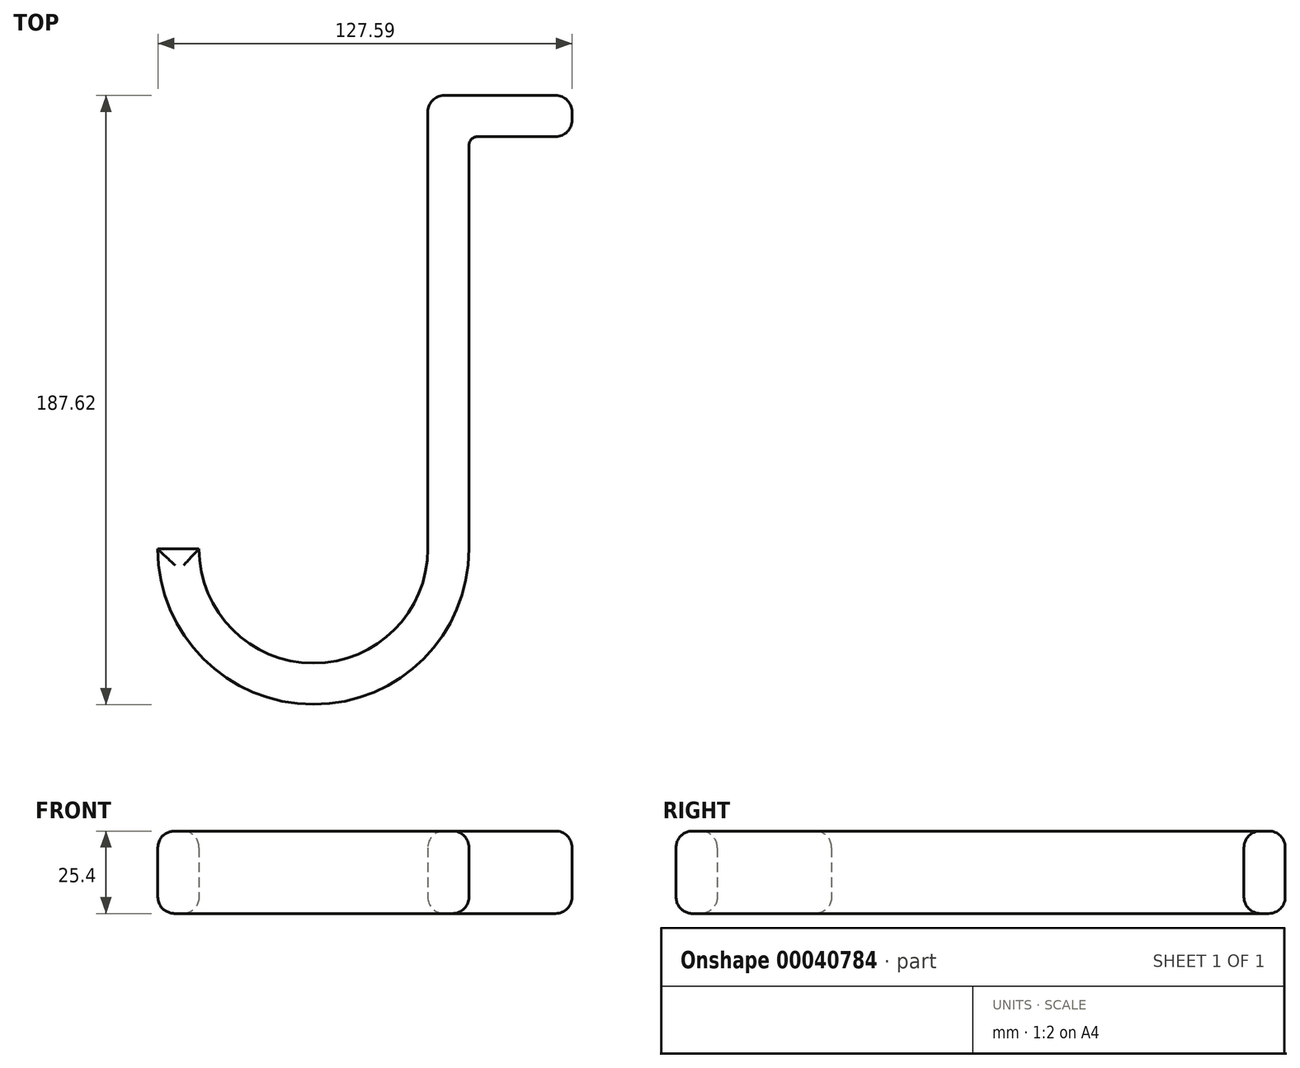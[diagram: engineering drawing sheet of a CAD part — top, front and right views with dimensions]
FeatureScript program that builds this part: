
annotation { "Feature Type Name" : "Feature", "Feature Type Description" : "" }
export const myFeature = defineFeature(function(context is Context, id is Id, definition is map)
    precondition{}
    {
        {
            var Q0;
            Q0=qCreatedBy(makeId("Top.planeOp"),FACE);
            var sketch = newSketch(context, id + "F0", { "sketchPlane" : qUnion([Q0])});
            skLineSegment(sketch, "E0.bottom", {"start": v(-7.23, 31.41) * mm, "end": v(5.47, 31.41) * mm});
            skLineSegment(sketch, "E0.left", {"start": v(-7.23, 31.41) * mm, "end": v(-7.23, -95.59) * mm});
            skLineSegment(sketch, "E0.right", {"start": v(5.47, 31.41) * mm, "end": v(5.47, -95.59) * mm});
            skLineSegment(sketch, "E1.bottom", {"start": v(-7.23, 44.11) * mm, "end": v(37.22, 44.11) * mm});
            skLineSegment(sketch, "E1.top", {"start": v(-7.23, 31.41) * mm, "end": v(37.22, 31.41) * mm});
            skLineSegment(sketch, "E1.left", {"start": v(-7.23, 44.11) * mm, "end": v(-7.23, 31.41) * mm});
            skLineSegment(sketch, "E1.right", {"start": v(37.22, 44.11) * mm, "end": v(37.22, 31.41) * mm});
            skLineSegment(sketch, "E2.bottom", {"start": v(24.52, 31.41) * mm, "end": v(37.22, 31.41) * mm});
            skLineSegment(sketch, "E2.top", {"start": v(24.52, -6.69) * mm, "end": v(37.22, -6.69) * mm});
            skLineSegment(sketch, "E2.left", {"start": v(24.52, 31.41) * mm, "end": v(24.52, -6.69) * mm});
            skLineSegment(sketch, "E2.right", {"start": v(37.22, 31.41) * mm, "end": v(37.22, -6.69) * mm});
            skArc(sketch, "E3", {"start": v(-77.67, -95.59) * mm, "mid": v(-42.45, -130.8) * mm, "end": v(-7.23, -95.59) * mm});
            skArc(sketch, "E4", {"start": v(-90.37, -95.59) * mm, "mid": v(-42.45, -143.5) * mm, "end": v(5.47, -95.59) * mm});
            skLineSegment(sketch, "E5", {"start": v(-77.67, -95.59) * mm, "end": v(-90.37, -95.59) * mm});
            skPoint(sketch, "E6.end.orphan", {"position": v(-42.45, -108.29) * mm});
            skSolve(sketch);
        }
        {
            var Q0;
            {var subQ1=sQuery(id+"F0.wireOp",EDGE,"E0.left");Q0=makeQuery(id+"F0.imprint","IMPRINT",FACE,{"disambiguationData":[TD([[makeQuery(id+"F0.imprint","IMPRINT",EDGE,{"derivedFrom":subQ1}),1.0]])]});}
            var Q1;
            Q1=makeQuery(id+"F0.imprint","IMPRINT",FACE,{"disambiguationData":[TD([[makeQuery(id+"F0.imprint","IMPRINT",EDGE,{"derivedFrom":sQuery(id+"F0.wireOp",EDGE,"E1.bottom")}),-1.0]])]});
            var Q2;
            Q2=makeQuery(id+"F0.imprint","IMPRINT",FACE,{"disambiguationData":[TD([[makeQuery(id+"F0.imprint","IMPRINT",EDGE,{"derivedFrom":sQuery(id+"F0.wireOp",EDGE,"E2.bottom")}),-1.0]])]});
            extrude(context, id + "F1", {"entities" : qUnion([Q0, Q1, Q2]), "depth" : 25.4 * mm});
        }
        {
            var Q0;
            Q0=makeQuery(id+"F1.opExtrude","SWEPT_EDGE",EDGE,{"disambiguationData":[OSD([sQuery(id+"F0.wireOp",EDGE,"E2.top"),sQuery(id+"F0.wireOp",EDGE,"E2.right")])]});
            var Q1;
            Q1=makeQuery(id+"F1.opExtrude","SWEPT_EDGE",EDGE,{"disambiguationData":[OSD([sQuery(id+"F0.wireOp",EDGE,"E2.top"),sQuery(id+"F0.wireOp",EDGE,"E2.left")])]});
            var Q2;
            Q2=makeQuery(id+"F1.opExtrude","SWEPT_EDGE",EDGE,{"disambiguationData":[OSD([sQuery(id+"F0.wireOp",EDGE,"E1.bottom"),sQuery(id+"F0.wireOp",EDGE,"E1.right")])]});
            var Q3;
            Q3=makeQuery(id+"F1.opExtrude","SWEPT_EDGE",EDGE,{"disambiguationData":[OSD([sQuery(id+"F0.wireOp",EDGE,"E1.bottom"),sQuery(id+"F0.wireOp",EDGE,"E1.left")])]});
            fillet(context, id + "F2", {"entities" : qUnion([Q0, Q1, Q2, Q3]), "radius" : 5.08 * mm, "tangentPropagation" : true, "allowEdgeOverflow" : false});
        }
        {
            var Q0;
            Q0=makeQuery(id+"F1.opExtrude","SWEPT_EDGE",EDGE,{"disambiguationData":[OSD([sQuery(id+"F0.wireOp",EDGE,"E0.right"),sQuery(id+"F0.wireOp",EDGE,"E1.top")])]});
            var Q1;
            Q1=makeQuery(id+"F1.opExtrude","SWEPT_EDGE",EDGE,{"disambiguationData":[OSD([sQuery(id+"F0.wireOp",EDGE,"E1.top"),sQuery(id+"F0.wireOp",EDGE,"E2.bottom"),sQuery(id+"F0.wireOp",EDGE,"E2.left")])]});
            fillet(context, id + "F3", {"entities" : qUnion([Q0, Q1]), "radius" : 2.54 * mm, "tangentPropagation" : true, "allowEdgeOverflow" : false});
        }
        {
            var Q0;
            Q0=makeQuery(id+"F1.opExtrude","CAP_FACE",FACE,{"disambiguationData":[OSD([sQuery(id+"F0.wireOp",EDGE,"E0.left"),sQuery(id+"F0.wireOp",EDGE,"E0.right"),sQuery(id+"F0.wireOp",EDGE,"E1.bottom"),sQuery(id+"F0.wireOp",EDGE,"E1.top"),sQuery(id+"F0.wireOp",EDGE,"E1.left"),sQuery(id+"F0.wireOp",EDGE,"E1.right"),sQuery(id+"F0.wireOp",EDGE,"E2.top"),sQuery(id+"F0.wireOp",EDGE,"E2.left"),sQuery(id+"F0.wireOp",EDGE,"E2.right"),sQuery(id+"F0.wireOp",EDGE,"E3"),sQuery(id+"F0.wireOp",EDGE,"E4"),sQuery(id+"F0.wireOp",EDGE,"E5")])],"isStart":false});
            var Q1;
            Q1=makeQuery(id+"F1.opExtrude","CAP_FACE",FACE,{"disambiguationData":[OSD([sQuery(id+"F0.wireOp",EDGE,"E0.left"),sQuery(id+"F0.wireOp",EDGE,"E0.right"),sQuery(id+"F0.wireOp",EDGE,"E1.bottom"),sQuery(id+"F0.wireOp",EDGE,"E1.top"),sQuery(id+"F0.wireOp",EDGE,"E1.left"),sQuery(id+"F0.wireOp",EDGE,"E1.right"),sQuery(id+"F0.wireOp",EDGE,"E2.top"),sQuery(id+"F0.wireOp",EDGE,"E2.left"),sQuery(id+"F0.wireOp",EDGE,"E2.right"),sQuery(id+"F0.wireOp",EDGE,"E3"),sQuery(id+"F0.wireOp",EDGE,"E4"),sQuery(id+"F0.wireOp",EDGE,"E5")])],"isStart":true});
            fillet(context, id + "F4", {"entities" : qUnion([Q0, Q1]), "radius" : 5.08 * mm, "tangentPropagation" : true, "allowEdgeOverflow" : false});
        }
    });
